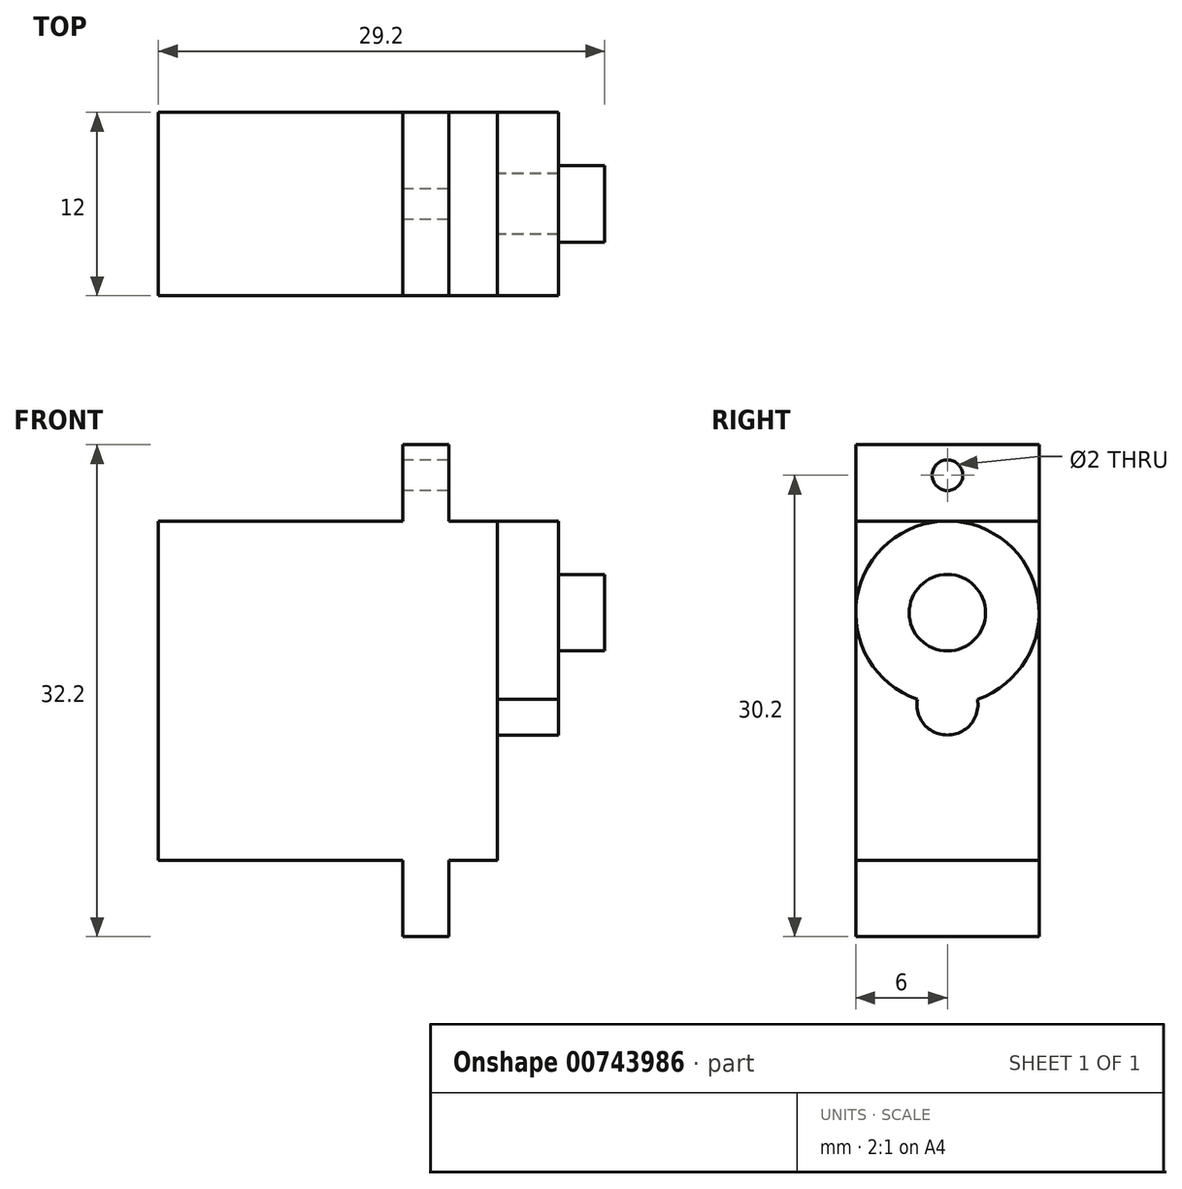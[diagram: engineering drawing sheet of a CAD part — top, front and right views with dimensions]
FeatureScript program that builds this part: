
annotation { "Feature Type Name" : "Feature", "Feature Type Description" : "" }
export const myFeature = defineFeature(function(context is Context, id is Id, definition is map)
    precondition{}
    {
        {
            var Q0;
            Q0=qCreatedBy(makeId("Top.planeOp"),FACE);
            var sketch = newSketch(context, id + "F0", { "sketchPlane" : qUnion([Q0])});
            skLineSegment(sketch, "E0", {"start": v(-46.06, 0) * mm, "end": v(53.34, 0) * mm, "construction": true});
            skLineSegment(sketch, "E1", {"start": v(0, 41.03) * mm, "end": v(0, -37.51) * mm, "construction": true});
            skLineSegment(sketch, "E2", {"start": v(-11.1, 0) * mm, "end": v(-11.1, 6) * mm});
            skLineSegment(sketch, "E3", {"start": v(-11.1, 6) * mm, "end": v(11.1, 6) * mm});
            skLineSegment(sketch, "E4", {"start": v(11.1, 6) * mm, "end": v(11.1, 0) * mm});
            skLineSegment(sketch, "E5.MirrorCS", {"start": v(-11.1, -6) * mm, "end": v(11.1, -6) * mm});
            skLineSegment(sketch, "E6.MirrorCS", {"start": v(-11.1, 0) * mm, "end": v(-11.1, -6) * mm});
            skLineSegment(sketch, "E7.MirrorCS", {"start": v(11.1, -6) * mm, "end": v(11.1, 0) * mm});
            skSolve(sketch);
        }
        {
            var Q0;
            Q0=makeQuery(id+"F0.imprint","IMPRINT",FACE,{"disambiguationData":[TD([[makeQuery(id+"F0.imprint","IMPRINT",EDGE,{"derivedFrom":sQuery(id+"F0.wireOp",EDGE,"E2")}),-1.0]])]});
            extrude(context, id + "F1", {"entities" : qUnion([Q0]), "depth" : 22.2 * mm, "offsetDistance" : 25 * mm});
        }
        {
            var Q0;
            Q0=makeQuery(id+"F1.opExtrude","CAP_FACE",FACE,{"disambiguationData":[OSD([sQuery(id+"F0.wireOp",EDGE,"E2"),sQuery(id+"F0.wireOp",EDGE,"E3"),sQuery(id+"F0.wireOp",EDGE,"E4"),sQuery(id+"F0.wireOp",EDGE,"E5.MirrorCS"),sQuery(id+"F0.wireOp",EDGE,"E6.MirrorCS"),sQuery(id+"F0.wireOp",EDGE,"E7.MirrorCS")])],"isStart":false});
            var sketch = newSketch(context, id + "F2", { "sketchPlane" : qUnion([Q0])});
            skLineSegment(sketch, "E8", {"start": v(4.9, 6) * mm, "end": v(4.9, -6) * mm});
            skLineSegment(sketch, "E9", {"start": v(0, 8.5) * mm, "end": v(0, -10.3) * mm, "construction": true});
            skLineSegment(sketch, "E10", {"start": v(4.9, -6) * mm, "end": v(7.9, -6) * mm});
            skLineSegment(sketch, "E11", {"start": v(7.9, -6) * mm, "end": v(7.9, 6) * mm});
            skLineSegment(sketch, "E12", {"start": v(7.9, 6) * mm, "end": v(4.9, 6) * mm});
            skSolve(sketch);
        }
        {
            var Q0;
            Q0=makeQuery(id+"F2.imprint","IMPRINT",FACE,{"disambiguationData":[TD([[makeQuery(id+"F2.imprint","IMPRINT",EDGE,{"derivedFrom":sQuery(id+"F2.wireOp",EDGE,"E8")}),1.0]])]});
            extrude(context, id + "F3", {"entities" : qUnion([Q0]), "operationType" : NewBodyOperationType.ADD, "depth" : 5 * mm, "offsetDistance" : 25 * mm});
        }
        {
            var Q0;
            Q0=makeQuery(id+"F1.opExtrude","CAP_FACE",FACE,{"disambiguationData":[OSD([sQuery(id+"F0.wireOp",EDGE,"E2"),sQuery(id+"F0.wireOp",EDGE,"E3"),sQuery(id+"F0.wireOp",EDGE,"E4"),sQuery(id+"F0.wireOp",EDGE,"E5.MirrorCS"),sQuery(id+"F0.wireOp",EDGE,"E6.MirrorCS"),sQuery(id+"F0.wireOp",EDGE,"E7.MirrorCS")])],"isStart":true});
            var sketch = newSketch(context, id + "F4", { "sketchPlane" : qUnion([Q0])});
            skLineSegment(sketch, "E13.0", {"start": v(4.9, 6) * mm, "end": v(7.9, 6) * mm});
            skLineSegment(sketch, "E14.0", {"start": v(7.9, 6) * mm, "end": v(7.9, -6) * mm});
            skLineSegment(sketch, "E15.0", {"start": v(4.9, -6) * mm, "end": v(7.9, -6) * mm});
            skLineSegment(sketch, "E16.0", {"start": v(4.9, -6) * mm, "end": v(4.9, 6) * mm});
            skSolve(sketch);
        }
        {
            var Q0;
            Q0=makeQuery(id+"F4.imprint","IMPRINT",FACE,{"disambiguationData":[TD([[makeQuery(id+"F4.imprint","IMPRINT",EDGE,{"derivedFrom":sQuery(id+"F4.wireOp",EDGE,"E13.0")}),-1.0]])]});
            extrude(context, id + "F5", {"entities" : qUnion([Q0]), "operationType" : NewBodyOperationType.ADD, "depth" : 5 * mm, "offsetDistance" : 25 * mm});
        }
        {
            var Q0;
            Q0=makeQuery(id+"F1.opExtrude","SWEPT_FACE",FACE,{"disambiguationData":[OSD([sQuery(id+"F0.wireOp",EDGE,"E4"),sQuery(id+"F0.wireOp",EDGE,"E7.MirrorCS")])]});
            var sketch = newSketch(context, id + "F6", { "sketchPlane" : qUnion([Q0])});
            skLineSegment(sketch, "E17", {"start": v(0, 28.5) * mm, "end": v(0, -4) * mm, "construction": true});
            skCircle(sketch, "E18", {"center": v(0, 16.2) * mm, "radius": 6 * mm});
            skCircle(sketch, "E19", {"center": v(0, 10.2) * mm, "radius": 2 * mm});
            skPoint(sketch, "E20", {"position": v(0, 22.2) * mm});
            skSolve(sketch);
        }
        {
            var Q0;
            Q0 = qSketchRegion(id + "F6", true);
            extrude(context, id + "F7", {"entities" : qUnion([Q0]), "operationType" : NewBodyOperationType.ADD, "depth" : 4 * mm, "offsetDistance" : 25 * mm});
        }
        {
            var Q0;
            Q0=makeQuery(id+"F7.opExtrude","CAP_FACE",FACE,{"disambiguationData":[OSD([sQuery(id+"F6.wireOp",EDGE,"E18")])],"isStart":false});
            var sketch = newSketch(context, id + "F8", { "sketchPlane" : qUnion([Q0])});
            skLineSegment(sketch, "E21", {"start": v(0, 23.02) * mm, "end": v(0, 8.7) * mm, "construction": true});
            skPoint(sketch, "E22", {"position": v(0, 10.2) * mm});
            skPoint(sketch, "E23", {"position": v(0, 22.2) * mm});
            skLineSegment(sketch, "E24", {"start": v(-7.15, 16.2) * mm, "end": v(8.84, 16.2) * mm, "construction": true});
            skCircle(sketch, "E25", {"center": v(0, 16.2) * mm, "radius": 2.5 * mm});
            skSolve(sketch);
        }
        {
            var Q0;
            Q0=makeQuery(id+"F8.imprint","IMPRINT",FACE,{"disambiguationData":[TD([[makeQuery(id+"F8.imprint","IMPRINT",EDGE,{"derivedFrom":sQuery(id+"F8.wireOp",EDGE,"E25")}),1.0]])]});
            extrude(context, id + "F9", {"entities" : qUnion([Q0]), "operationType" : NewBodyOperationType.ADD, "depth" : 3 * mm, "offsetDistance" : 25 * mm});
        }
        {
            var Q0;
            Q0=makeQuery(id+"F3.opExtrude","SWEPT_FACE",FACE,{"disambiguationData":[OSD([sQuery(id+"F2.wireOp",EDGE,"E8")])]});
            var sketch = newSketch(context, id + "F10", { "sketchPlane" : qUnion([Q0])});
            skCircle(sketch, "E26", {"center": v(0, 25.2) * mm, "radius": 1 * mm});
            skLineSegment(sketch, "E27.0", {"start": v(-6, 22.2) * mm, "end": v(6, 22.2) * mm});
            skLineSegment(sketch, "E28.0", {"start": v(-6, 0) * mm, "end": v(6, 0) * mm});
            skLineSegment(sketch, "E29", {"start": v(-11.44, 11.1) * mm, "end": v(14.6, 11.1) * mm, "construction": true});
            skCircle(sketch, "E30.MirrorC", {"center": v(0, -3) * mm, "radius": 1 * mm});
            skSolve(sketch);
        }
        {
            var Q0;
            Q0=makeQuery(id+"F10.imprint","IMPRINT",FACE,{"disambiguationData":[TD([[makeQuery(id+"F10.imprint","IMPRINT",EDGE,{"derivedFrom":sQuery(id+"F10.wireOp",EDGE,"E26")}),1.0]])]});
            var Q1;
            Q1=makeQuery(id+"F10.imprint","IMPRINT",FACE,{"disambiguationData":[TD([[makeQuery(id+"F10.imprint","IMPRINT",EDGE,{"derivedFrom":sQuery(id+"F10.wireOp",EDGE,"E30.MirrorC")}),-1.0]])]});
            extrude(context, id + "F11", {"entities" : qUnion([Q0, Q1]), "operationType" : NewBodyOperationType.REMOVE, "oppositeDirection" : true, "depth" : 25 * mm, "offsetDistance" : 25 * mm});
        }
    });
